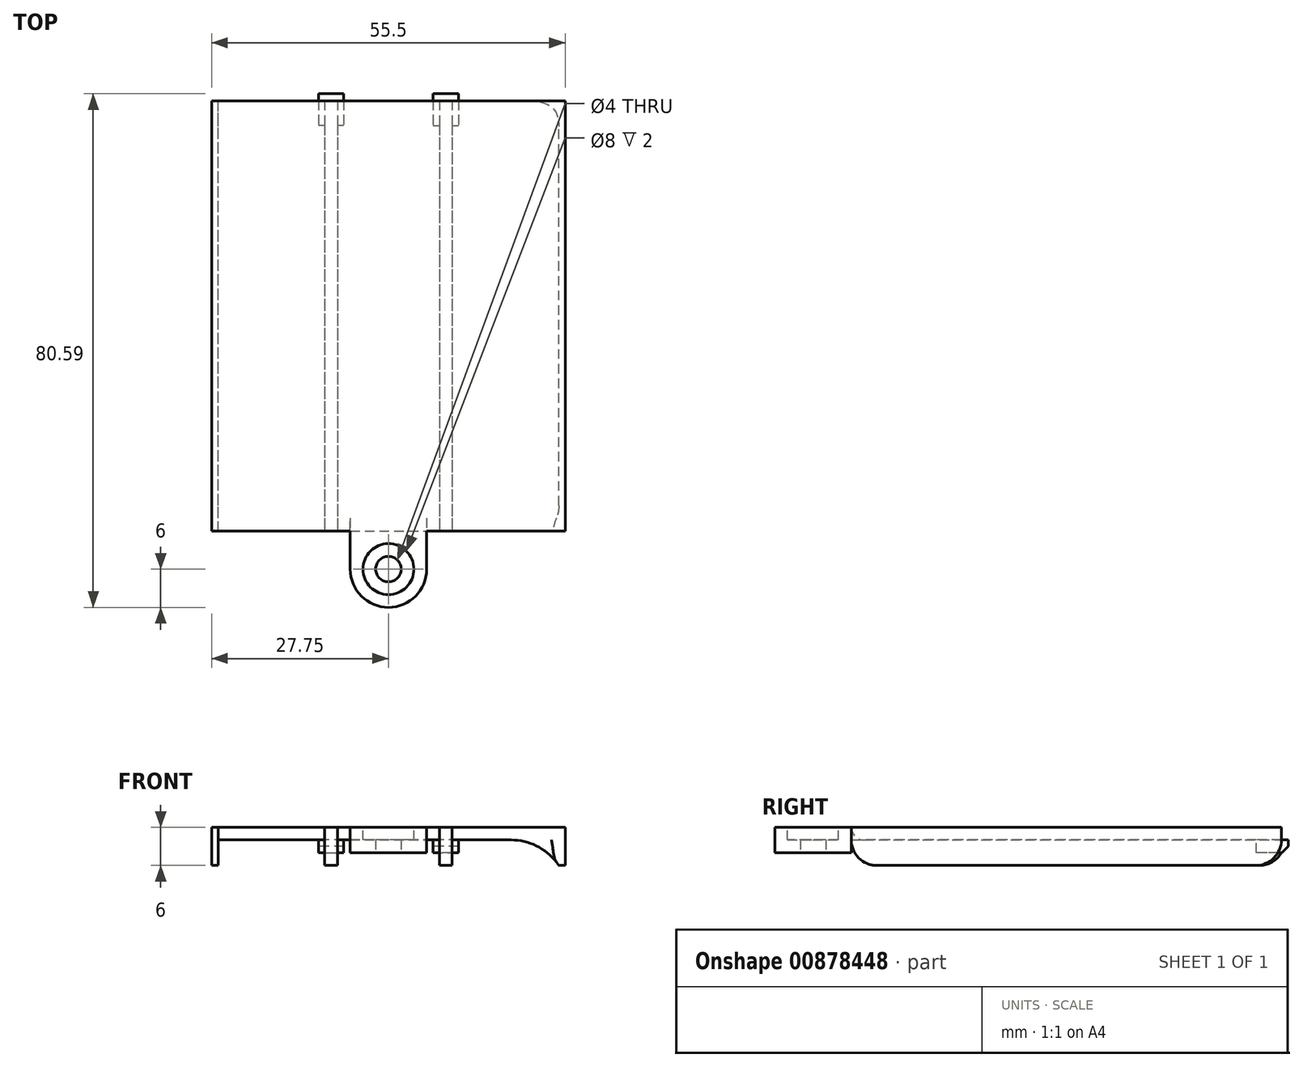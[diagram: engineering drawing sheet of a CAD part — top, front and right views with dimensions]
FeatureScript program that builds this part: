
annotation { "Feature Type Name" : "Feature", "Feature Type Description" : "" }
export const myFeature = defineFeature(function(context is Context, id is Id, definition is map)
    precondition{}
    {
        {
            var Q0;
            Q0=qCreatedBy(makeId("Top.planeOp"),FACE);
            var sketch = newSketch(context, id + "F0", { "sketchPlane" : qUnion([Q0])});
            skLineSegment(sketch, "E0.bottom", {"start": v(27.75, 33.75) * mm, "end": v(-27.75, 33.75) * mm});
            skLineSegment(sketch, "E0.top", {"start": v(27.75, -33.75) * mm, "end": v(0, -33.75) * mm});
            skLineSegment(sketch, "E0.left", {"start": v(27.75, 33.75) * mm, "end": v(27.75, -33.75) * mm});
            skLineSegment(sketch, "E0.right", {"start": v(-27.75, 33.75) * mm, "end": v(-27.75, -33.75) * mm});
            skPoint(sketch, "E0.middle", {"position": v(0, 0) * mm});
            skLineSegment(sketch, "E1", {"start": v(0, -33.75) * mm, "end": v(-27.75, -33.75) * mm});
            skSolve(sketch);
        }
        {
            var Q0;
            Q0=makeQuery(id+"F0.imprint","IMPRINT",FACE,{"disambiguationData":[TD([[makeQuery(id+"F0.imprint","IMPRINT",EDGE,{"derivedFrom":sQuery(id+"F0.wireOp",EDGE,"E0.bottom")}),1.0]])]});
            extrude(context, id + "F1", {"entities" : qUnion([Q0]), "depth" : 2 * mm, "offsetDistance" : 25 * mm});
        }
        {
            var Q0;
            Q0=qCreatedBy(makeId("Top.planeOp"),FACE);
            var sketch = newSketch(context, id + "F2", { "sketchPlane" : qUnion([Q0])});
            skLineSegment(sketch, "E2", {"start": v(-9, 42.2) * mm, "end": v(-9, 22.33) * mm, "construction": true});
            skLineSegment(sketch, "E3.MirrorCS", {"start": v(9, 42.2) * mm, "end": v(9, 22.33) * mm, "construction": true});
            skLineSegment(sketch, "E4.bottom", {"start": v(-7, 34.84) * mm, "end": v(-11, 34.84) * mm});
            skLineSegment(sketch, "E4.top", {"start": v(-7, 29.84) * mm, "end": v(-11, 29.84) * mm});
            skLineSegment(sketch, "E4.left", {"start": v(-7, 34.84) * mm, "end": v(-7, 29.84) * mm});
            skLineSegment(sketch, "E4.right", {"start": v(-11, 34.84) * mm, "end": v(-11, 29.84) * mm});
            skPoint(sketch, "E4.middle", {"position": v(-9, 32.34) * mm});
            skLineSegment(sketch, "E5.MirrorCS", {"start": v(7, 29.84) * mm, "end": v(11, 29.84) * mm});
            skLineSegment(sketch, "E6.MirrorCS", {"start": v(11, 34.84) * mm, "end": v(11, 29.84) * mm});
            skPoint(sketch, "E7.MirrorP", {"position": v(9, 32.34) * mm});
            skLineSegment(sketch, "E8.MirrorCS", {"start": v(7, 34.84) * mm, "end": v(11, 34.84) * mm});
            skLineSegment(sketch, "E9.MirrorCS", {"start": v(7, 34.84) * mm, "end": v(7, 29.84) * mm});
            skSolve(sketch);
        }
        {
            var Q0;
            Q0 = qSketchRegion(id + "F2", true);
            extrude(context, id + "F3", {"entities" : qUnion([Q0]), "operationType" : NewBodyOperationType.ADD, "oppositeDirection" : true, "depth" : 2 * mm, "offsetDistance" : 25 * mm});
        }
        {
            var Q0;
            Q0=makeQuery(id+"F1.opExtrude","CAP_FACE",FACE,{"disambiguationData":[OSD([sQuery(id+"F0.wireOp",EDGE,"E0.bottom"),sQuery(id+"F0.wireOp",EDGE,"E0.top"),sQuery(id+"F0.wireOp",EDGE,"E0.left"),sQuery(id+"F0.wireOp",EDGE,"E0.right"),sQuery(id+"F0.wireOp",EDGE,"E1"),sQuery(id+"F0.wireOp",EDGE,"bL2IQ40Q-TqVf-k89g-JyY6-6n1qcl0WTyE6.left"),sQuery(id+"F0.wireOp",EDGE,"bL2IQ40Q-TqVf-k89g-JyY6-6n1qcl0WTyE6.right"),sQuery(id+"F0.wireOp",EDGE,"e0833dff-2275-40e9-923f-619383ae2fc2.filletArc"),sQuery(id+"F0.wireOp",EDGE,"5f5ede43-ec16-4103-a103-03ff5000ae76.filletArc"),sQuery(id+"F0.wireOp",EDGE,"7HOMQQT8-eHA4-BbJ3-2D6r-BTUmNwNOhEWS")])],"isStart":true});
            var sketch = newSketch(context, id + "F4", { "sketchPlane" : qUnion([Q0])});
            skLineSegment(sketch, "E10.bottom", {"start": v(-27.75, 33.75) * mm, "end": v(-26.75, 33.75) * mm});
            skLineSegment(sketch, "E10.top", {"start": v(-27.75, -33.75) * mm, "end": v(-26.75, -33.75) * mm});
            skLineSegment(sketch, "E10.left", {"start": v(-27.75, 33.75) * mm, "end": v(-27.75, -33.75) * mm});
            skLineSegment(sketch, "E10.right", {"start": v(-26.75, 33.75) * mm, "end": v(-26.75, -33.75) * mm});
            skLineSegment(sketch, "E11.MirrorCS", {"start": v(27.75, -33.75) * mm, "end": v(26.75, -33.75) * mm});
            skLineSegment(sketch, "E12.MirrorCS", {"start": v(26.75, 33.75) * mm, "end": v(26.75, -33.75) * mm});
            skLineSegment(sketch, "E13.MirrorCS", {"start": v(27.75, 33.75) * mm, "end": v(27.75, -33.75) * mm});
            skLineSegment(sketch, "E14.MirrorCS", {"start": v(27.75, 33.75) * mm, "end": v(26.75, 33.75) * mm});
            skLineSegment(sketch, "E15.bottom", {"start": v(10, -33.75) * mm, "end": v(8, -33.75) * mm});
            skLineSegment(sketch, "E15.top", {"start": v(10, 33.74) * mm, "end": v(8, 33.74) * mm});
            skLineSegment(sketch, "E15.left", {"start": v(10, -33.75) * mm, "end": v(10, 33.74) * mm});
            skLineSegment(sketch, "E15.right", {"start": v(8, -33.75) * mm, "end": v(8, 33.74) * mm});
            skPoint(sketch, "E15.middle", {"position": v(9, 0) * mm});
            skLineSegment(sketch, "E16.MirrorCS", {"start": v(-10, -33.75) * mm, "end": v(-8, -33.75) * mm});
            skLineSegment(sketch, "E17.MirrorCS", {"start": v(-10, 33.74) * mm, "end": v(-8, 33.74) * mm});
            skPoint(sketch, "E18.MirrorP", {"position": v(-9, 0) * mm});
            skLineSegment(sketch, "E19.MirrorCS", {"start": v(-10, -33.75) * mm, "end": v(-10, 33.74) * mm});
            skLineSegment(sketch, "E20.MirrorCS", {"start": v(-8, -33.75) * mm, "end": v(-8, 33.74) * mm});
            skSolve(sketch);
        }
        {
            var Q0;
            Q0 = qSketchRegion(id + "F4", true);
            extrude(context, id + "F5", {"entities" : qUnion([Q0]), "operationType" : NewBodyOperationType.ADD, "depth" : 4 * mm, "offsetDistance" : 25 * mm});
        }
        {
            var Q0;
            Q0=makeQuery(id+"F5.opExtrude","CAP_EDGE",EDGE,{"disambiguationData":[OSD([sQuery(id+"F4.wireOp",EDGE,"E10.right")])],"isStart":true});
            var Q1;
            Q1=makeQuery(id+"F5.opExtrude","CAP_EDGE",EDGE,{"disambiguationData":[OSD([sQuery(id+"F4.wireOp",EDGE,"E12.MirrorCS")])],"isStart":true});
            fillet(context, id + "F6", {"entities" : qUnion([Q0, Q1]), "radius" : 9 * mm, "tangentPropagation" : true, "allowEdgeOverflow" : false});
        }
        {
            var Q0;
            Q0=makeQuery(id+"F5.opExtrude","CAP_EDGE",EDGE,{"disambiguationData":[OSD([sQuery(id+"F4.wireOp",EDGE,"E10.top")])],"isStart":false});
            var Q1;
            Q1=makeQuery(id+"F5.opExtrude","CAP_EDGE",EDGE,{"disambiguationData":[OSD([sQuery(id+"F4.wireOp",EDGE,"E16.MirrorCS")])],"isStart":false});
            var Q2;
            Q2=makeQuery(id+"F5.opExtrude","CAP_EDGE",EDGE,{"disambiguationData":[OSD([sQuery(id+"F4.wireOp",EDGE,"E15.bottom")])],"isStart":false});
            var Q3;
            Q3=makeQuery(id+"F5.opExtrude","CAP_EDGE",EDGE,{"disambiguationData":[OSD([sQuery(id+"F4.wireOp",EDGE,"E14.MirrorCS")])],"isStart":false});
            var Q4;
            Q4=makeQuery(id+"F5.opExtrude","CAP_EDGE",EDGE,{"disambiguationData":[OSD([sQuery(id+"F4.wireOp",EDGE,"E15.top")])],"isStart":false});
            var Q5;
            Q5=makeQuery(id+"F5.opExtrude","CAP_EDGE",EDGE,{"disambiguationData":[OSD([sQuery(id+"F4.wireOp",EDGE,"E17.MirrorCS")])],"isStart":false});
            var Q6;
            Q6=makeQuery(id+"F5.opExtrude","CAP_EDGE",EDGE,{"disambiguationData":[OSD([sQuery(id+"F4.wireOp",EDGE,"E10.bottom")])],"isStart":false});
            var Q7;
            Q7=makeQuery(id+"F5.opExtrude","CAP_EDGE",EDGE,{"disambiguationData":[OSD([sQuery(id+"F4.wireOp",EDGE,"E11.MirrorCS")])],"isStart":false});
            fillet(context, id + "F7", {"entities" : qUnion([Q0, Q1, Q2, Q3, Q4, Q5, Q6, Q7]), "radius" : 4 * mm, "tangentPropagation" : true, "allowEdgeOverflow" : false});
        }
        {
            var Q0;
            Q0=makeQuery(id+"F3.opExtrude","CAP_EDGE",EDGE,{"disambiguationData":[OSD([sQuery(id+"F2.wireOp",EDGE,"E4.bottom")])],"isStart":false});
            var Q1;
            Q1=makeQuery(id+"F3.opExtrude","CAP_EDGE",EDGE,{"disambiguationData":[OSD([sQuery(id+"F2.wireOp",EDGE,"E8.MirrorCS")])],"isStart":false});
            chamfer(context, id + "F8", {"entities" : qUnion([Q0, Q1]), "width" : 1 * mm, "tangentPropagation" : true});
        }
        {
            var Q0;
            Q0=qCreatedBy(makeId("Top.planeOp"),FACE);
            var sketch = newSketch(context, id + "F9", { "sketchPlane" : qUnion([Q0])});
            skLineSegment(sketch, "E21.bottom", {"start": v(0, -45.75) * mm, "end": v(0, -45.75) * mm});
            skLineSegment(sketch, "E21.top", {"start": v(6, -33.75) * mm, "end": v(-6, -33.75) * mm});
            skLineSegment(sketch, "E21.left", {"start": v(6, -39.75) * mm, "end": v(6, -33.75) * mm});
            skLineSegment(sketch, "E21.right", {"start": v(-6, -39.75) * mm, "end": v(-6, -33.75) * mm});
            skPoint(sketch, "E21.middle", {"position": v(0, -39.75) * mm});
            skPoint(sketch, "E22.visualSharp", {"position": v(-6, -45.75) * mm});
            skArc(sketch, "E22.filletArc", {"start": v(-6, -39.75) * mm, "mid": v(-4.24, -44) * mm, "end": v(0, -45.75) * mm});
            skPoint(sketch, "E23.visualSharp", {"position": v(6, -45.75) * mm});
            skArc(sketch, "E23.filletArc", {"start": v(0, -45.75) * mm, "mid": v(4.24, -44) * mm, "end": v(6, -39.75) * mm});
            skCircle(sketch, "E24", {"center": v(0, -39.75) * mm, "radius": 2 * mm});
            skLineSegment(sketch, "E25", {"start": v(-11.06, -41.65) * mm, "end": v(7.41, -41.65) * mm, "construction": true});
            skSolve(sketch);
        }
        {
            var Q0;
            Q0 = qSketchRegion(id + "F9", true);
            extrude(context, id + "F10", {"entities" : qUnion([Q0]), "operationType" : NewBodyOperationType.ADD, "depth" : 2 * mm, "offsetDistance" : 25 * mm, "hasSecondDirection" : true, "secondDirectionOppositeDirection" : true, "secondDirectionDepth" : 2 * mm});
        }
        {
            var Q0;
            {var subQ0=sQuery(id+"F0.wireOp",EDGE,"E1");var subQ1=sQuery(id+"F0.wireOp",EDGE,"E0.top");var subQ2=makeQuery(id+"F1.opExtrude","CAP_FACE",FACE,{"disambiguationData":[OSD([sQuery(id+"F0.wireOp",EDGE,"E0.bottom"),subQ1,sQuery(id+"F0.wireOp",EDGE,"E0.left"),sQuery(id+"F0.wireOp",EDGE,"E0.right"),subQ0])],"isStart":true});var subQ3=makeQuery(id+"F5.opExtrude","SWEPT_FACE",FACE,{"disambiguationData":[OSD([sQuery(id+"F4.wireOp",EDGE,"E10.bottom")])]});var subQ4=makeQuery(id+"F5.opExtrude","SWEPT_FACE",FACE,{"disambiguationData":[OSD([sQuery(id+"F4.wireOp",EDGE,"E14.MirrorCS")])]});var subQ5=makeQuery(id+"F1.opExtrude","SWEPT_FACE",FACE,{"disambiguationData":[OSD([subQ1,subQ0])]});var subQ7=sQuery(id+"F4.wireOp",EDGE,"E15.right");Q0=makeQuery(id+"F10.boolean.opBoolean","SPLIT",EDGE,{"disambiguationData":[topologyDisambiguationEdgeConnected([subQ2,makeQuery(id+"F10.opExtrude","SWEPT_FACE",FACE,{"disambiguationData":[OSD([sQuery(id+"F9.wireOp",EDGE,"E21.top")])]})])],"derivedFrom":makeQuery(id+"F5.boolean.opBoolean","SPLIT",EDGE,{"disambiguationData":[topologyDisambiguationEdgeConnected([subQ2,subQ5,subQ3,subQ4]),TD([makeQuery(id+"F5.opExtrude","SWEPT_FACE",FACE,{"disambiguationData":[OSD([subQ7])]})])],"derivedFrom":makeQuery(id+"F1.opExtrude","CAP_EDGE",EDGE,{"disambiguationData":[OSD([subQ1,subQ0])],"isStart":true})})});}
            fillet(context, id + "F11", {"entities" : qUnion([Q0]), "radius" : 2 * mm, "tangentPropagation" : true, "allowEdgeOverflow" : false});
        }
        {
            var Q0;
            Q0=makeQuery(id+"F10.boolean.opBoolean","MERGE",FACE,{"derivedFrom":[makeQuery(id+"F1.opExtrude","CAP_FACE",FACE,{"disambiguationData":[OSD([sQuery(id+"F0.wireOp",EDGE,"E0.bottom"),sQuery(id+"F0.wireOp",EDGE,"E0.top"),sQuery(id+"F0.wireOp",EDGE,"E0.left"),sQuery(id+"F0.wireOp",EDGE,"E0.right"),sQuery(id+"F0.wireOp",EDGE,"E1")])],"isStart":false}),makeQuery(id+"F10.opExtrude","CAP_FACE",FACE,{"disambiguationData":[OSD([sQuery(id+"F9.wireOp",EDGE,"E21.top"),sQuery(id+"F9.wireOp",EDGE,"E21.left"),sQuery(id+"F9.wireOp",EDGE,"E21.right"),sQuery(id+"F9.wireOp",EDGE,"E22.filletArc"),sQuery(id+"F9.wireOp",EDGE,"E23.filletArc"),sQuery(id+"F9.wireOp",EDGE,"E24")])],"isStart":false})]});
            var sketch = newSketch(context, id + "F12", { "sketchPlane" : qUnion([Q0])});
            skCircle(sketch, "E26", {"center": v(0, -39.75) * mm, "radius": 4 * mm});
            skSolve(sketch);
        }
        {
            var Q0;
            Q0 = qSketchRegion(id + "F12", true);
            extrude(context, id + "F13", {"entities" : qUnion([Q0]), "operationType" : NewBodyOperationType.REMOVE, "oppositeDirection" : true, "depth" : 2 * mm, "offsetDistance" : 25 * mm});
        }
    });
